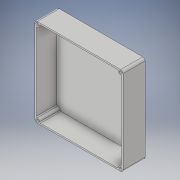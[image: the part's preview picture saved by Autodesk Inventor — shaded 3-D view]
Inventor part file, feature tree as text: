
AUTODESK INVENTOR PART (.ipt)
format: ipt  version: 2019.4 (Build 234330000, 330)  size: 244,224 bytes
history: native  units: mm
features: extrude x9, fillet x3, sketch x1
ambient origin geometry x8: Origin, YZ Plane, XZ Plane, XY Plane, X Axis, Y Axis, Z Axis, Center Point
bodies: Solid1 (feature_tree)
feature tree (13):
  sketch  "Sketch1"  dims[d0=150.0mm d1=150.0mm d2=145.0mm d3=145.0mm d4=2.5mm d5=0.0mm d6=37.5mm d7=0.0mm d8=4.0mm d9=4.0mm d10=5.0mm d11=40.0mm d13=360.0deg d15=40.0mm d17=360.0deg d19=37.5mm d20=0.0mm d21=37.5mm d22=0.0mm d23=35.5mm d24=0.0mm d25=1.5mm d26=40.0mm d28=360.0deg d30=37.5mm d31=0.0mm d32=37.5mm d33=0.0mm d34=2.5mm d35=0.0mm d36=35.5mm d37=0.0mm d38=4.0mm d39=4.0mm d40=1.5mm]
  extrude  "Extrusion1"  Depth=150.0mm
  extrude  "Extrusion2"  Depth=145.0mm
  extrude  "Extrusion3"  Depth=145.0mm
  extrude  "Extrusion4"  Depth=2.5mm TaperAngle=0.0deg
  extrude  "Extrusion5"  Depth=37.5mm TaperAngle=0.0deg
  extrude  "Extrusion6"  Depth=4.0mm
  extrude  "Extrusion7"  Depth=4.0mm
  extrude  "Extrusion8"  Depth=1.5mm
  extrude  "Extrusion9"  Depth=1.5mm TaperAngle=360.0deg
  fillet  "Fillet1"  Radius=40.0mm
  fillet  "Fillet2"  Radius=37.5mm
  fillet  "Fillet3"  Radius=37.5mm
